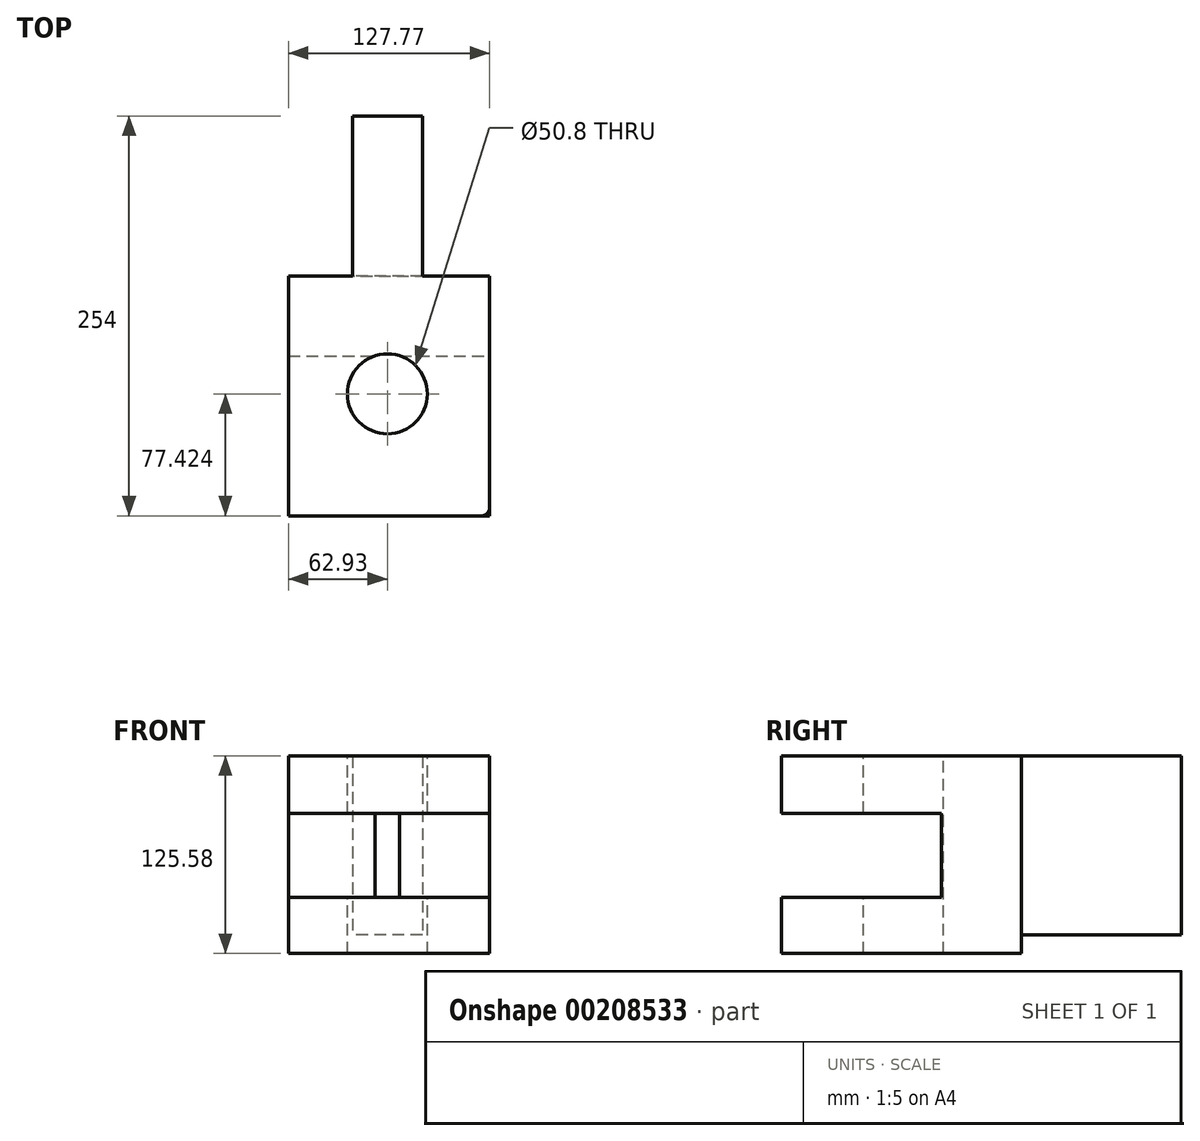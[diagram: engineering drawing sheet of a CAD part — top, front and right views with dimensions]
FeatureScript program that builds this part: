
annotation { "Feature Type Name" : "Feature", "Feature Type Description" : "" }
export const myFeature = defineFeature(function(context is Context, id is Id, definition is map)
    precondition{}
    {
        {
            var Q0;
            Q0=qCreatedBy(makeId("Front.planeOp"),FACE);
            var sketch = newSketch(context, id + "F0", { "sketchPlane" : qUnion([Q0])});
            skLineSegment(sketch, "E0", {"start": v(-49.08, 42.35) * mm, "end": v(76.97, 42.35) * mm});
            skLineSegment(sketch, "E1.bottom", {"start": v(-62.93, 21.88) * mm, "end": v(64.84, 21.88) * mm});
            skLineSegment(sketch, "E1.top", {"start": v(-62.93, -103.7) * mm, "end": v(64.84, -103.7) * mm});
            skLineSegment(sketch, "E1.left", {"start": v(-62.93, 21.88) * mm, "end": v(-62.93, -103.7) * mm});
            skLineSegment(sketch, "E1.right", {"start": v(64.84, 21.88) * mm, "end": v(64.84, -103.7) * mm});
            skSolve(sketch);
        }
        {
            var Q0;
            Q0=makeQuery(id+"F0.imprint","IMPRINT",FACE,{"disambiguationData":[TD([[makeQuery(id+"F0.imprint","IMPRINT",EDGE,{"derivedFrom":sQuery(id+"F0.wireOp",EDGE,"E1.bottom")}),-1.0]])]});
            extrude(context, id + "F1", {"entities" : qUnion([Q0]), "depth" : 50.8 * mm});
        }
        {
            var Q0;
            Q0=makeQuery(id+"F1.opExtrude","CAP_FACE",FACE,{"disambiguationData":[OSD([sQuery(id+"F0.wireOp",EDGE,"E1.bottom"),sQuery(id+"F0.wireOp",EDGE,"E1.top"),sQuery(id+"F0.wireOp",EDGE,"E1.left"),sQuery(id+"F0.wireOp",EDGE,"E1.right")])],"isStart":false});
            var sketch = newSketch(context, id + "F2", { "sketchPlane" : qUnion([Q0])});
            skLineSegment(sketch, "E2.bottom", {"start": v(-62.93, 21.88) * mm, "end": v(64.84, 21.88) * mm});
            skLineSegment(sketch, "E2.top", {"start": v(-62.93, -14.67) * mm, "end": v(64.84, -14.67) * mm});
            skLineSegment(sketch, "E2.left", {"start": v(-62.93, 21.88) * mm, "end": v(-62.93, -14.67) * mm});
            skLineSegment(sketch, "E2.right", {"start": v(64.84, 21.88) * mm, "end": v(64.84, -14.67) * mm});
            skLineSegment(sketch, "E3.bottom", {"start": v(-62.93, -103.7) * mm, "end": v(64.84, -103.7) * mm});
            skLineSegment(sketch, "E3.top", {"start": v(-62.93, -68) * mm, "end": v(64.84, -68) * mm});
            skLineSegment(sketch, "E3.left", {"start": v(-62.93, -103.7) * mm, "end": v(-62.93, -68) * mm});
            skLineSegment(sketch, "E3.right", {"start": v(64.84, -103.7) * mm, "end": v(64.84, -68) * mm});
            skSolve(sketch);
        }
        {
            var Q0;
            Q0=makeQuery(id+"F2.imprint","IMPRINT",FACE,{"disambiguationData":[TD([[makeQuery(id+"F2.imprint","IMPRINT",EDGE,{"derivedFrom":sQuery(id+"F2.wireOp",EDGE,"E2.bottom")}),-1.0]])]});
            var Q1;
            Q1=makeQuery(id+"F2.imprint","IMPRINT",FACE,{"disambiguationData":[TD([[makeQuery(id+"F2.imprint","IMPRINT",EDGE,{"derivedFrom":sQuery(id+"F2.wireOp",EDGE,"E3.bottom")}),1.0]])]});
            extrude(context, id + "F3", {"entities" : qUnion([Q0, Q1]), "operationType" : NewBodyOperationType.ADD, "depth" : 101.6 * mm});
        }
        {
            var Q0;
            Q0=makeQuery(id+"F3.boolean.opBoolean","MERGE",FACE,{"derivedFrom":[makeQuery(id+"F1.opExtrude","SWEPT_FACE",FACE,{"disambiguationData":[OSD([sQuery(id+"F0.wireOp",EDGE,"E1.bottom")])]}),makeQuery(id+"F3.opExtrude","SWEPT_FACE",FACE,{"disambiguationData":[OSD([sQuery(id+"F2.wireOp",EDGE,"E2.bottom")])]})]});
            var sketch = newSketch(context, id + "F4", { "sketchPlane" : qUnion([Q0])});
            skPoint(sketch, "E4", {"position": v(0, -74.98) * mm});
            skSolve(sketch);
        }
        {
            var Q0;
            Q0=sQuery(id+"F4.wireOp",VERTEX,"E4");
            var Q1;
            Q1=makeQuery(id+"F1.opExtrude","SWEPT_BODY",BODY,{"disambiguationData":[OSD([sQuery(id+"F0.wireOp",EDGE,"E1.bottom"),sQuery(id+"F0.wireOp",EDGE,"E1.top"),sQuery(id+"F0.wireOp",EDGE,"E1.left"),sQuery(id+"F0.wireOp",EDGE,"E1.right")])]});
            hole(context, id + "F5", {"style" : HoleStyle.SIMPLE, "endStyle" : HoleEndStyle.THROUGH, "holeDiameter" : 50.8 * mm, "locations" : qUnion([Q0]), "scope" : qUnion([Q1]), "isTappedThrough" : true});
        }
        {
            var Q0;
            Q0=makeQuery(id+"F3.opExtrude","CAP_EDGE",EDGE,{"disambiguationData":[OSD([sQuery(id+"F2.wireOp",EDGE,"E2.right")])],"isStart":false});
            fillet(context, id + "F6", {"entities" : qUnion([Q0]), "radius" : 5.08 * mm, "tangentPropagation" : true, "allowEdgeOverflow" : false});
        }
        {
            var Q0;
            Q0=makeQuery(id+"F1.opExtrude","CAP_FACE",FACE,{"disambiguationData":[OSD([sQuery(id+"F0.wireOp",EDGE,"E1.bottom"),sQuery(id+"F0.wireOp",EDGE,"E1.top"),sQuery(id+"F0.wireOp",EDGE,"E1.left"),sQuery(id+"F0.wireOp",EDGE,"E1.right")])],"isStart":true});
            var sketch = newSketch(context, id + "F7", { "sketchPlane" : qUnion([Q0])});
            skLineSegment(sketch, "E5.bottom", {"start": v(-22.24, 21.88) * mm, "end": v(22.24, 21.88) * mm});
            skLineSegment(sketch, "E5.top", {"start": v(-22.24, -91.71) * mm, "end": v(22.24, -91.71) * mm});
            skLineSegment(sketch, "E5.left", {"start": v(-22.24, 21.88) * mm, "end": v(-22.24, -91.71) * mm});
            skLineSegment(sketch, "E5.right", {"start": v(22.24, 21.88) * mm, "end": v(22.24, -91.71) * mm});
            skPoint(sketch, "E5.middle", {"position": v(0, -34.92) * mm});
            skSolve(sketch);
        }
        {
            var Q0;
            Q0=makeQuery(id+"F7.imprint","IMPRINT",FACE,{"disambiguationData":[TD([[makeQuery(id+"F7.imprint","IMPRINT",EDGE,{"derivedFrom":sQuery(id+"F7.wireOp",EDGE,"E5.bottom")}),1.0]])]});
            extrude(context, id + "F8", {"entities" : qUnion([Q0]), "operationType" : NewBodyOperationType.ADD, "depth" : 101.6 * mm});
        }
    });
